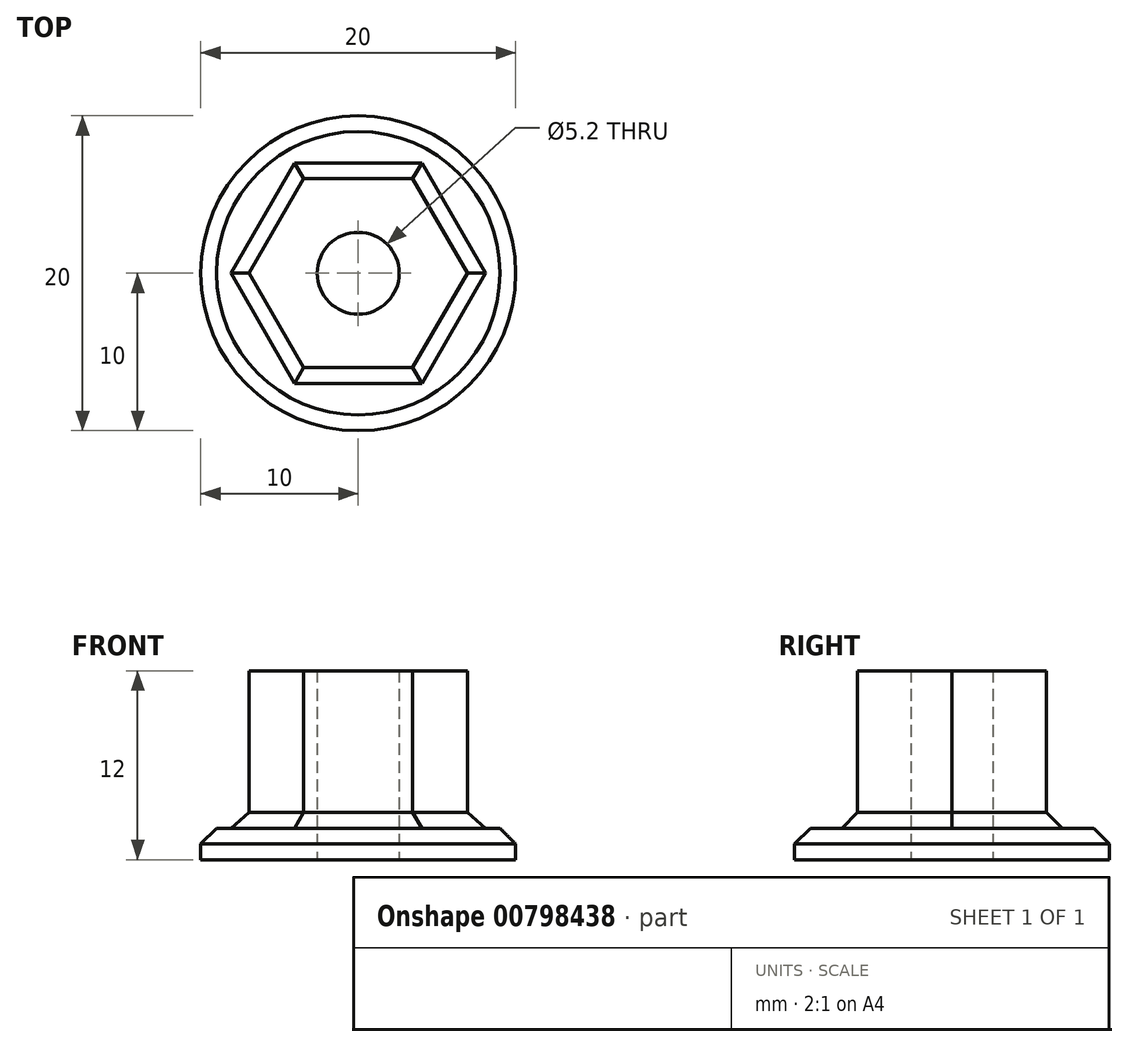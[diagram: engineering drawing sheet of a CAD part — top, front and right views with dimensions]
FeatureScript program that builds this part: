
annotation { "Feature Type Name" : "Feature", "Feature Type Description" : "" }
export const myFeature = defineFeature(function(context is Context, id is Id, definition is map)
    precondition{}
    {
        {
            var Q0;
            Q0=qCreatedBy(makeId("Top.planeOp"),FACE);
            var sketch = newSketch(context, id + "F0", { "sketchPlane" : qUnion([Q0])});
            skCircle(sketch, "E0.cCircle", {"center": v(0, 0) * mm, "radius": 6 * mm, "construction": true});
            skLineSegment(sketch, "E0.0", {"start": v(-3.46, 6) * mm, "end": v(3.46, 6) * mm});
            skLineSegment(sketch, "E0.1", {"start": v(3.46, 6) * mm, "end": v(6.93, 0) * mm});
            skLineSegment(sketch, "E0.2", {"start": v(6.93, 0) * mm, "end": v(3.46, -6) * mm});
            skLineSegment(sketch, "E0.3", {"start": v(3.46, -6) * mm, "end": v(-3.46, -6) * mm});
            skLineSegment(sketch, "E0.4", {"start": v(-3.46, -6) * mm, "end": v(-6.93, 0) * mm});
            skLineSegment(sketch, "E0.5", {"start": v(-6.93, 0) * mm, "end": v(-3.46, 6) * mm});
            skPoint(sketch, "E0.0.midPoint", {"position": v(0, 6) * mm});
            skSolve(sketch);
        }
        {
            var Q0;
            Q0=makeQuery(id+"F0.imprint","IMPRINT",FACE,{"disambiguationData":[TD([[makeQuery(id+"F0.imprint","IMPRINT",EDGE,{"derivedFrom":sQuery(id+"F0.wireOp",EDGE,"E0.0")}),-1.0]])]});
            extrude(context, id + "F1", {"entities" : qUnion([Q0]), "depth" : 12 * mm, "offsetDistance" : 25 * mm});
        }
        {
            var Q0;
            Q0=qCreatedBy(makeId("Top.planeOp"),FACE);
            var sketch = newSketch(context, id + "F2", { "sketchPlane" : qUnion([Q0])});
            skCircle(sketch, "E1", {"center": v(0, 0) * mm, "radius": 10 * mm});
            skCircle(sketch, "E2", {"center": v(0, 0) * mm, "radius": 2.6 * mm});
            skCircle(sketch, "E3", {"center": v(0, 0) * mm, "radius": 4.6 * mm});
            skSolve(sketch);
        }
        {
            var Q0;
            Q0 = qSketchRegion(id + "F2", true);
            extrude(context, id + "F3", {"entities" : qUnion([Q0]), "operationType" : NewBodyOperationType.ADD, "depth" : 2 * mm, "offsetDistance" : 25 * mm});
        }
        {
            var Q0;
            Q0=makeQuery(id+"F2.imprint","IMPRINT",FACE,{"disambiguationData":[TD([[makeQuery(id+"F2.imprint","IMPRINT",EDGE,{"derivedFrom":sQuery(id+"F2.wireOp",EDGE,"E2")}),1.0]])]});
            extrude(context, id + "F4", {"entities" : qUnion([Q0]), "operationType" : NewBodyOperationType.REMOVE, "endBound" : BoundingType.THROUGH_ALL, "depth" : 25 * mm, "offsetDistance" : 25 * mm});
        }
        {
            var Q0;
            Q0=makeQuery(id+"F3.opExtrude","CAP_FACE",FACE,{"disambiguationData":[OSD([sQuery(id+"F2.wireOp",EDGE,"E1"),sQuery(id+"F2.wireOp",EDGE,"E3")])],"isStart":false});
            chamfer(context, id + "F5", {"entities" : qUnion([Q0]), "width" : 1 * mm, "tangentPropagation" : true});
        }
    });
